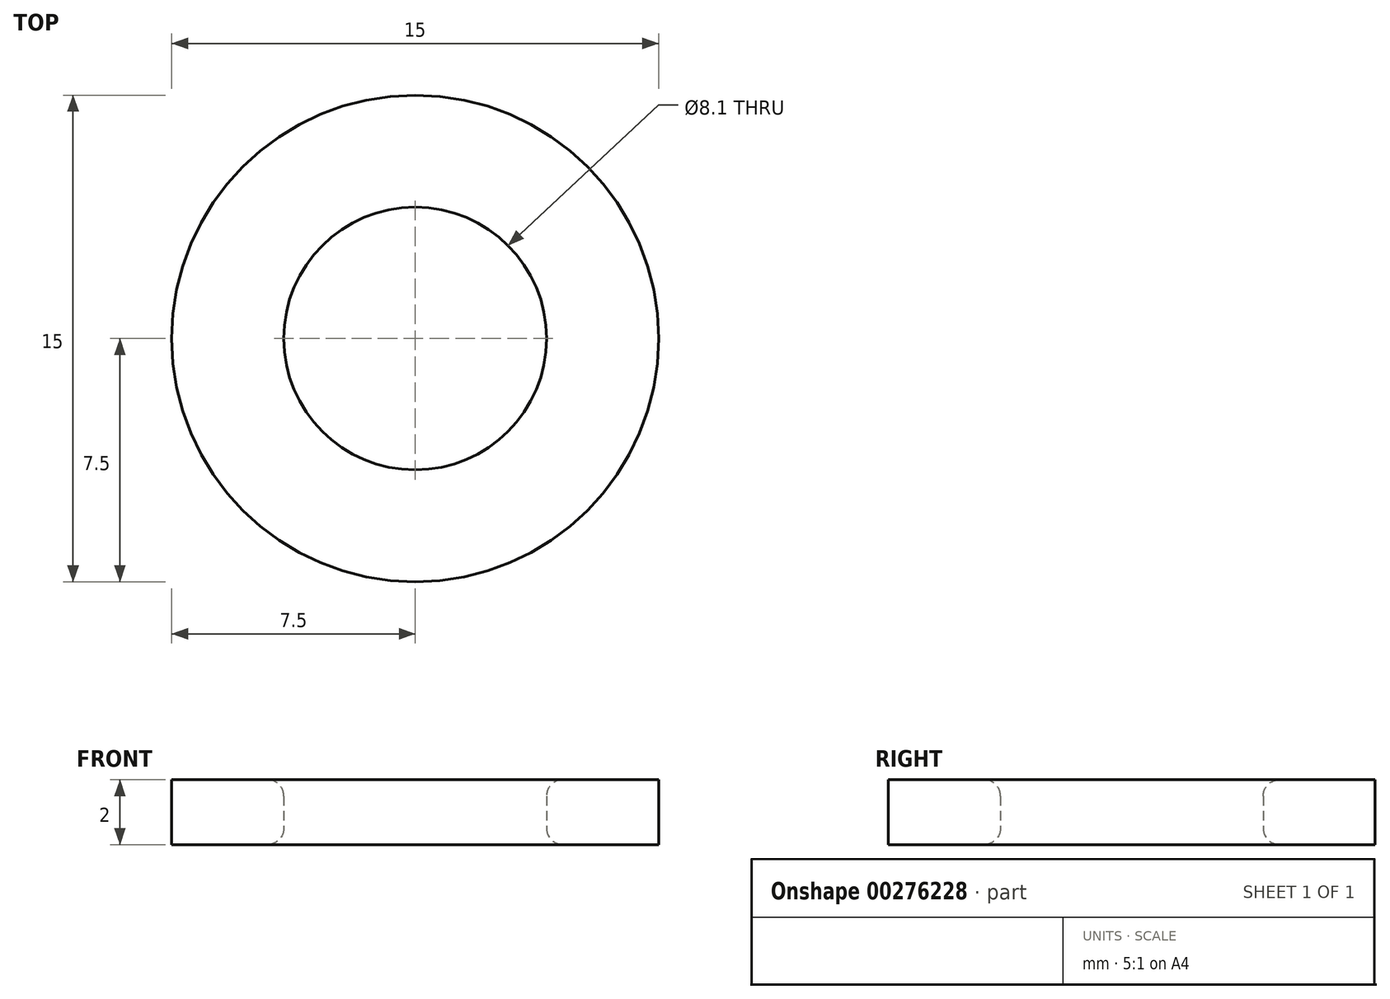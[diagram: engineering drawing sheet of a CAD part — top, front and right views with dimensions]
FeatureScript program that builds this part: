
annotation { "Feature Type Name" : "Feature", "Feature Type Description" : "" }
export const myFeature = defineFeature(function(context is Context, id is Id, definition is map)
    precondition{}
    {
        {
            var Q0;
            Q0=qCreatedBy(makeId("Top.planeOp"),FACE);
            var sketch = newSketch(context, id + "F0", { "sketchPlane" : qUnion([Q0])});
            skCircle(sketch, "E0", {"center": v(0, 0) * mm, "radius": 4.05 * mm});
            skCircle(sketch, "E1", {"center": v(0, 0) * mm, "radius": 7.5 * mm});
            skSolve(sketch);
        }
        {
            var Q0;
            Q0=makeQuery(id+"F0.imprint","IMPRINT",FACE,{"disambiguationData":[TD([[makeQuery(id+"F0.imprint","IMPRINT",EDGE,{"derivedFrom":sQuery(id+"F0.wireOp",EDGE,"E0")}),-1.0]])]});
            extrude(context, id + "F1", {"entities" : qUnion([Q0]), "depth" : 2 * mm});
        }
        {
            var Q0;
            Q0=makeQuery(id+"F1.opExtrude","CAP_EDGE",EDGE,{"disambiguationData":[OSD([sQuery(id+"F0.wireOp",EDGE,"E0")])],"isStart":false});
            var Q1;
            Q1=makeQuery(id+"F1.opExtrude","CAP_EDGE",EDGE,{"disambiguationData":[OSD([sQuery(id+"F0.wireOp",EDGE,"E0")])],"isStart":true});
            fillet(context, id + "F2", {"entities" : qUnion([Q0, Q1]), "radius" : .5 * mm, "tangentPropagation" : true, "allowEdgeOverflow" : false});
        }
    });
